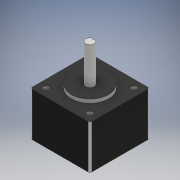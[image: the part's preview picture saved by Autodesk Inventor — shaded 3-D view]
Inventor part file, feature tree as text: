
AUTODESK INVENTOR PART (.ipt)
format: ipt  version: 2018.3 (Build 223284000, 284)  size: 139,776 bytes
history: native  units: mm
features: sketch x4, extrude x4, other x1, hole x1, fillet x1
ambient origin geometry x8: Origin, YZ Plane, XZ Plane, XY Plane, X Axis, Y Axis, Z Axis, Center Point
bodies: Body1 (feature_tree)
feature tree (11):
  other  "Твердое тело1"
  sketch  "Эскиз1"
  extrude  "Выдавливание1"  Depth=35.2mm
  extrude  "Выдавливание2"  Depth=35.2mm
  extrude  "Выдавливание3"  Depth=26.0mm TaperAngle=0.0deg
  extrude  "Выдавливание4"  Depth=22.0mm
  hole  "Отверстие1"  [1 undecoded]
  fillet  "Сопряжение1"  Radius=5.0mm
  sketch  "Эскиз2"
  sketch  "Эскиз3"
  sketch  "Эскиз4"
note: 1 required parameter value undecoded (feature->parameter linkage not recoverable at this tier; creation-order binding heuristic only, values carry confidence <= 0.55)
